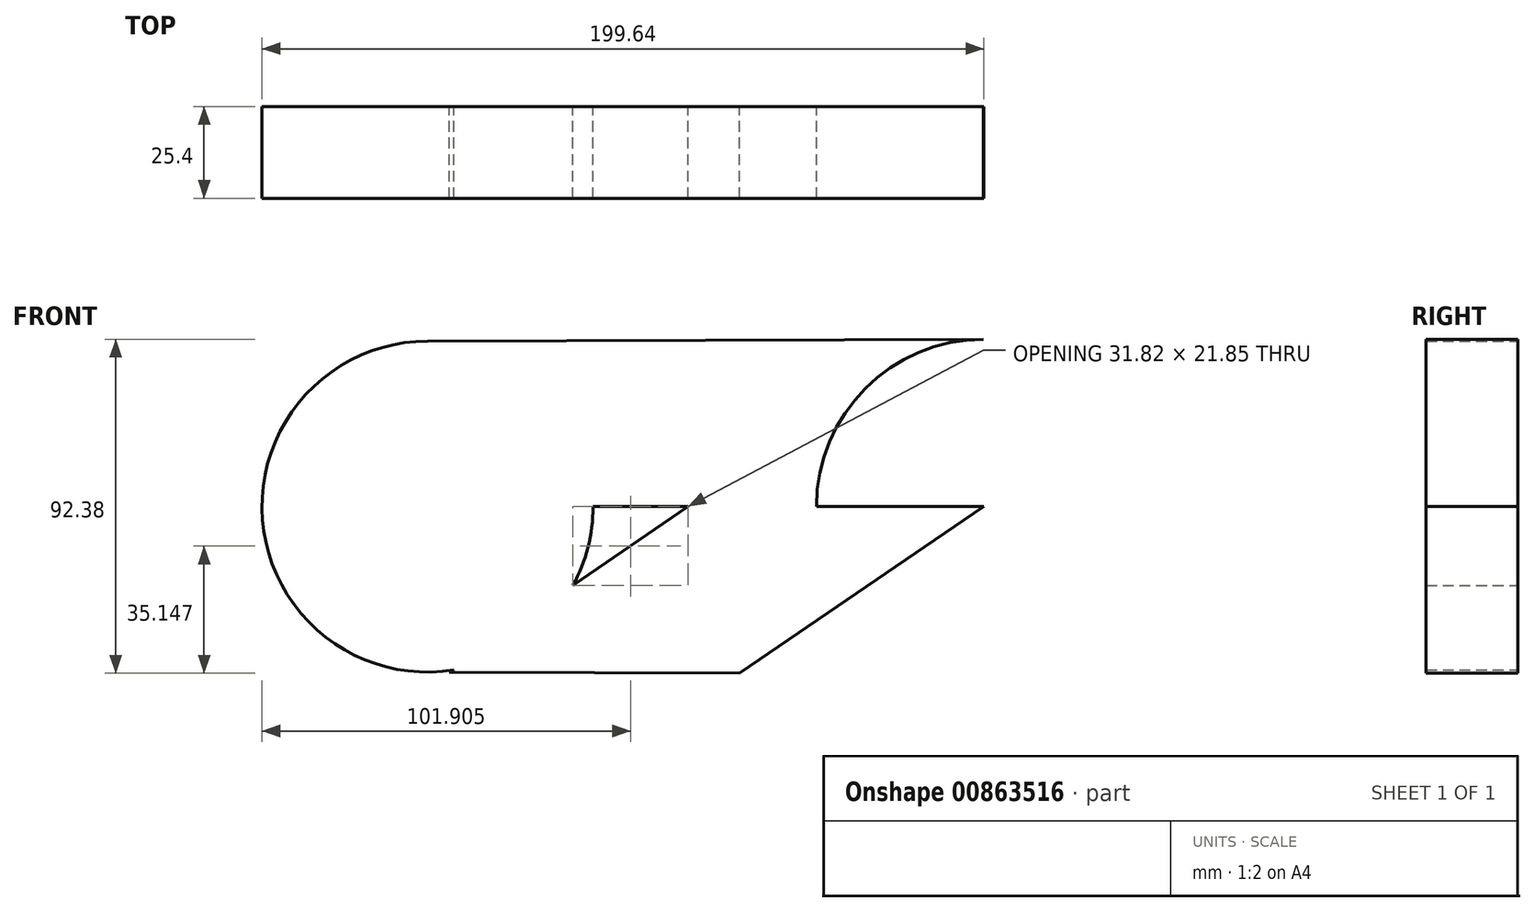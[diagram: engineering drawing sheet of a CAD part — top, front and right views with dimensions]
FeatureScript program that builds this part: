
annotation { "Feature Type Name" : "Feature", "Feature Type Description" : "" }
export const myFeature = defineFeature(function(context is Context, id is Id, definition is map)
    precondition{}
    {
        {
            var Q0;
            Q0=qCreatedBy(makeId("Front.planeOp"),FACE);
            var sketch = newSketch(context, id + "F0", { "sketchPlane" : qUnion([Q0])});
            skCircle(sketch, "E0", {"center": v(0, 0) * mm, "radius": 45.77 * mm});
            skCircle(sketch, "E1", {"center": v(153.87, 0) * mm, "radius": 46.3 * mm});
            skLineSegment(sketch, "E2", {"start": v(0, 45.77) * mm, "end": v(153.7, 46.3) * mm});
            skLineSegment(sketch, "E3", {"start": v(0, -45.77) * mm, "end": v(153.7, -46.3) * mm});
            skLineSegment(sketch, "E4", {"start": v(0, 0) * mm, "end": v(153.87, 0) * mm});
            skLineSegment(sketch, "E5", {"start": v(19.4, -41.46) * mm, "end": v(153.87, 0) * mm, "construction": true});
            skLineSegment(sketch, "E6", {"start": v(19.4, -41.46) * mm, "end": v(0, -45.77) * mm, "construction": true});
            skLineSegment(sketch, "E7.MirrorCS", {"start": v(26.71, -86.64) * mm, "end": v(153.87, 0) * mm});
            skLineSegment(sketch, "E8.MirrorCS", {"start": v(0.94, -48.82) * mm, "end": v(127.66, 38.18) * mm});
            skCircle(sketch, "E9.MirrorC", {"center": v(26.71, -86.64) * mm, "radius": 45.77 * mm});
            skLineSegment(sketch, "E10.MirrorCS", {"start": v(52.49, -124.47) * mm, "end": v(179.81, -38.36) * mm});
            skSolve(sketch);
        }
        {
            var Q0;
            {var subQ0=sQuery(id+"F0.wireOp",EDGE,"E9.MirrorC");var subQ1=sQuery(id+"F0.wireOp",EDGE,"E0");var subQ2=makeQuery(id+"F0.imprint","INTERSECT",VERTEX,{"disambiguationData":[OD(1.0)],"derivedFrom":[subQ1,subQ0]});Q0=makeQuery(id+"F0.imprint","IMPRINT",FACE,{"disambiguationData":[TD([[makeQuery(id+"F0.imprint","IMPRINT",EDGE,{"disambiguationData":[TD([[subQ2,-1.0]])],"derivedFrom":subQ1}),-1.0]])]});}
            var Q1;
            {var subQ0=sQuery(id+"F0.wireOp",EDGE,"E8.MirrorCS");var subQ1=sQuery(id+"F0.wireOp",EDGE,"E4");var subQ2=makeQuery(id+"F0.imprint","INTERSECT",VERTEX,{"derivedFrom":[subQ1,subQ0]});Q1=makeQuery(id+"F0.imprint","IMPRINT",FACE,{"disambiguationData":[TD([[makeQuery(id+"F0.imprint","IMPRINT",EDGE,{"disambiguationData":[TD([[subQ2,-1.0]])],"derivedFrom":subQ1}),1.0]])]});}
            var Q2;
            {var subQ0=sQuery(id+"F0.wireOp",EDGE,"E9.MirrorC");var subQ1=sQuery(id+"F0.wireOp",EDGE,"E0");var subQ2=makeQuery(id+"F0.imprint","INTERSECT",VERTEX,{"disambiguationData":[OD(0.0)],"derivedFrom":[subQ1,subQ0]});Q2=makeQuery(id+"F0.imprint","IMPRINT",FACE,{"disambiguationData":[TD([[makeQuery(id+"F0.imprint","IMPRINT",EDGE,{"disambiguationData":[TD([[subQ2,-1.0]])],"derivedFrom":subQ1}),-1.0]])]});}
            var Q3;
            {var subQ0=sQuery(id+"F0.wireOp",EDGE,"E9.MirrorC");var subQ6=makeQuery(id+"F0.imprint","INTERSECT",VERTEX,{"derivedFrom":[subQ0,sQuery(id+"F0.wireOp",EDGE,"E10.MirrorCS")]});Q3=makeQuery(id+"F0.imprint","IMPRINT",FACE,{"disambiguationData":[TD([[makeQuery(id+"F0.imprint","IMPRINT",EDGE,{"disambiguationData":[TD([[subQ6,1.0]])],"derivedFrom":subQ0}),-1.0]])]});}
            var Q4;
            {var subQ0=sQuery(id+"F0.wireOp",EDGE,"E7.MirrorCS");var subQ1=sQuery(id+"F0.wireOp",EDGE,"E4");var subQ2=makeQuery(id+"F0.imprint","INTERSECT",VERTEX,{"derivedFrom":[subQ1,subQ0]});Q4=makeQuery(id+"F0.imprint","IMPRINT",FACE,{"disambiguationData":[TD([[makeQuery(id+"F0.imprint","IMPRINT",EDGE,{"disambiguationData":[TD([[subQ2,1.0]])],"derivedFrom":subQ1}),-1.0]])]});}
            var Q5;
            {var subQ0=sQuery(id+"F0.wireOp",EDGE,"E0");var subQ6=makeQuery(id+"F0.imprint","INTERSECT",VERTEX,{"derivedFrom":[subQ0,sQuery(id+"F0.wireOp",EDGE,"E2")]});Q5=makeQuery(id+"F0.imprint","IMPRINT",FACE,{"disambiguationData":[TD([[makeQuery(id+"F0.imprint","IMPRINT",EDGE,{"disambiguationData":[TD([[subQ6,1.0]])],"derivedFrom":subQ0}),1.0]])]});}
            var Q6;
            {var subQ6=sQuery(id+"F0.wireOp",EDGE,"E2");Q6=makeQuery(id+"F0.imprint","IMPRINT",FACE,{"disambiguationData":[TD([[makeQuery(id+"F0.imprint","IMPRINT",EDGE,{"derivedFrom":subQ6}),-1.0]])]});}
            var Q7;
            {var subQ0=sQuery(id+"F0.wireOp",EDGE,"E8.MirrorCS");var subQ1=sQuery(id+"F0.wireOp",EDGE,"E0");var subQ2=makeQuery(id+"F0.imprint","INTERSECT",VERTEX,{"disambiguationData":[OD(0.0)],"derivedFrom":[subQ1,subQ0]});Q7=makeQuery(id+"F0.imprint","IMPRINT",FACE,{"disambiguationData":[TD([[makeQuery(id+"F0.imprint","IMPRINT",EDGE,{"disambiguationData":[TD([[subQ2,-1.0]])],"derivedFrom":subQ1}),1.0]])]});}
            var Q8;
            {var subQ0=sQuery(id+"F0.wireOp",EDGE,"E9.MirrorC");var subQ1=sQuery(id+"F0.wireOp",EDGE,"E0");var subQ2=makeQuery(id+"F0.imprint","INTERSECT",VERTEX,{"disambiguationData":[OD(0.0)],"derivedFrom":[subQ1,subQ0]});Q8=makeQuery(id+"F0.imprint","IMPRINT",FACE,{"disambiguationData":[TD([[makeQuery(id+"F0.imprint","IMPRINT",EDGE,{"disambiguationData":[TD([[subQ2,-1.0]])],"derivedFrom":subQ1}),1.0]])]});}
            extrude(context, id + "F1", {"entities" : qUnion([Q0, Q1, Q2, Q3, Q4, Q5, Q6, Q7, Q8]), "depth" : 25.4 * mm, "offsetDistance" : 25.4 * mm});
        }
    });
